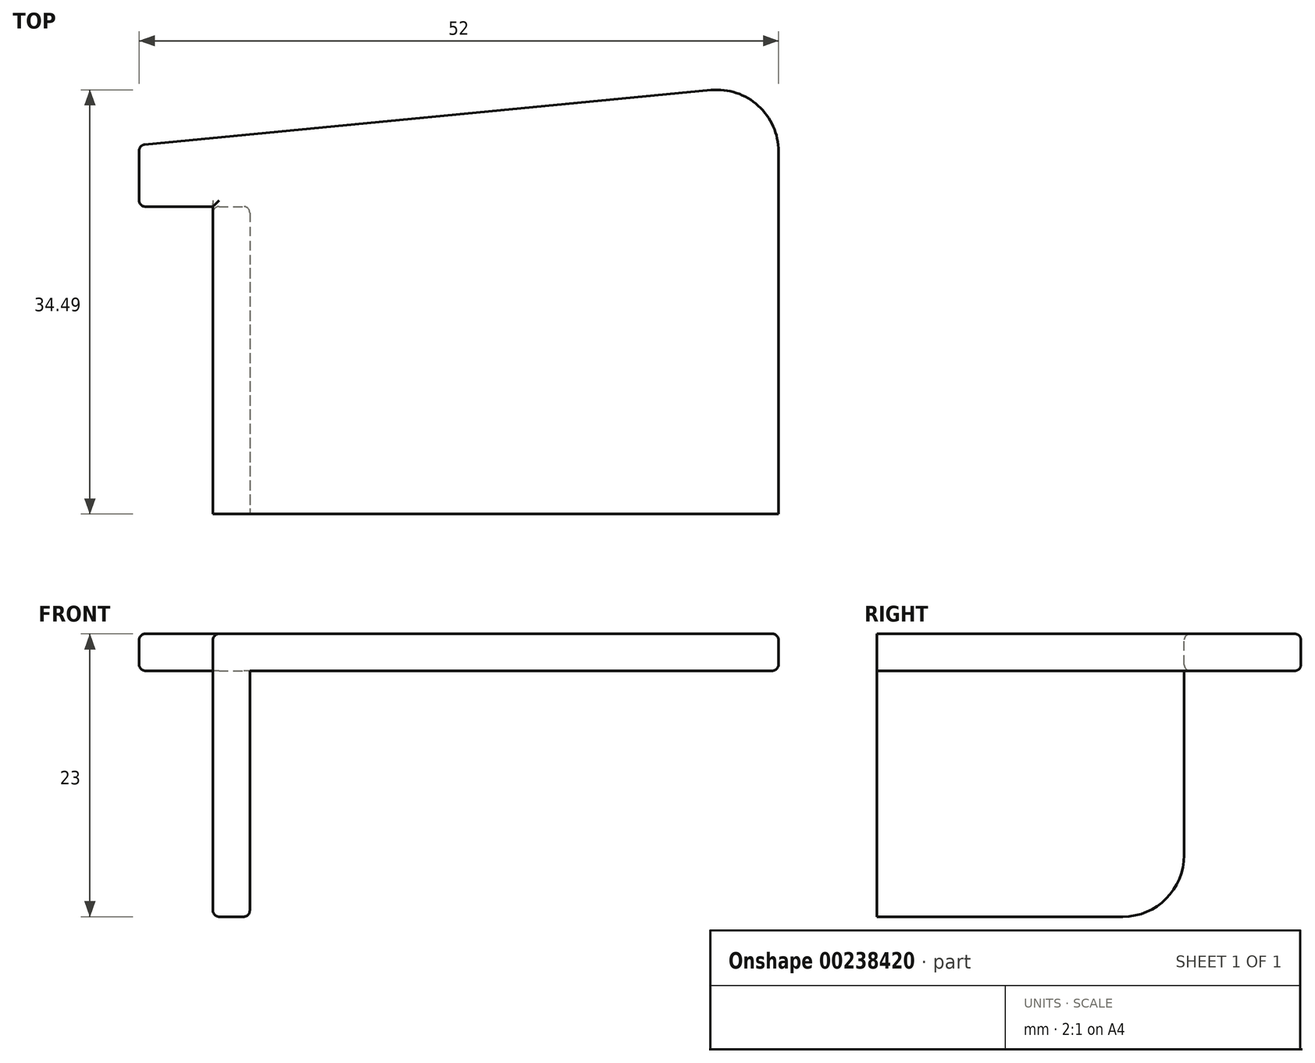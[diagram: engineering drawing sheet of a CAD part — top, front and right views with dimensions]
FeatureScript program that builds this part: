
annotation { "Feature Type Name" : "Feature", "Feature Type Description" : "" }
export const myFeature = defineFeature(function(context is Context, id is Id, definition is map)
    precondition{}
    {
        {
            var Q0;
            Q0=qCreatedBy(makeId("Top.planeOp"),FACE);
            var sketch = newSketch(context, id + "F0", { "sketchPlane" : qUnion([Q0])});
            skLineSegment(sketch, "E0", {"start": v(-20.55, 9.84) * mm, "end": v(-20.55, 4.84) * mm});
            skLineSegment(sketch, "E1", {"start": v(-20.55, 4.84) * mm, "end": v(-14.55, 4.84) * mm});
            skLineSegment(sketch, "E2", {"start": v(-14.55, 4.84) * mm, "end": v(-14.55, -20.16) * mm});
            skLineSegment(sketch, "E3", {"start": v(-14.55, -20.16) * mm, "end": v(31.45, -20.16) * mm});
            skLineSegment(sketch, "E4", {"start": v(31.45, -20.16) * mm, "end": v(31.45, 9.33) * mm});
            skLineSegment(sketch, "E5", {"start": v(-20.55, 9.84) * mm, "end": v(25.97, 14.31) * mm});
            skPoint(sketch, "E6.visualSharp", {"position": v(31.45, 14.84) * mm});
            skArc(sketch, "E6.filletArc", {"start": v(31.45, 9.33) * mm, "mid": v(29.8, 13.03) * mm, "end": v(25.97, 14.31) * mm});
            skLineSegment(sketch, "E7.bottom", {"start": v(-14.55, 4.84) * mm, "end": v(-11.55, 4.84) * mm});
            skLineSegment(sketch, "E7.top", {"start": v(-14.55, -20.16) * mm, "end": v(-11.55, -20.16) * mm});
            skLineSegment(sketch, "E7.right", {"start": v(-11.55, 4.84) * mm, "end": v(-11.55, -20.16) * mm});
            skSolve(sketch);
        }
        {
            var Q0;
            Q0=makeQuery(id+"F0.imprint","IMPRINT",FACE,{"disambiguationData":[TD([[makeQuery(id+"F0.imprint","IMPRINT",EDGE,{"derivedFrom":sQuery(id+"F0.wireOp",EDGE,"E0")}),1.0]])]});
            extrude(context, id + "F1", {"entities" : qUnion([Q0]), "oppositeDirection" : true, "depth" : 3 * mm, "offsetDistance" : 25 * mm});
        }
        {
            var Q0;
            {var subQ0=sQuery(id+"F0.wireOp",EDGE,"E2");Q0=makeQuery(id+"F0.imprint","IMPRINT",FACE,{"disambiguationData":[TD([[makeQuery(id+"F0.imprint","IMPRINT",EDGE,{"derivedFrom":subQ0}),1.0]])]});}
            extrude(context, id + "F2", {"entities" : qUnion([Q0]), "operationType" : NewBodyOperationType.ADD, "oppositeDirection" : true, "depth" : 23 * mm, "offsetDistance" : 25 * mm});
        }
        {
            var Q0;
            Q0=makeQuery(id+"F1.opExtrude","CAP_EDGE",EDGE,{"disambiguationData":[OSD([sQuery(id+"F0.wireOp",EDGE,"E5")])],"isStart":true});
            var Q1;
            Q1=makeQuery(id+"F1.opExtrude","CAP_EDGE",EDGE,{"disambiguationData":[OSD([sQuery(id+"F0.wireOp",EDGE,"E5")])],"isStart":false});
            var Q2;
            Q2=makeQuery(id+"F1.opExtrude","SWEPT_EDGE",EDGE,{"disambiguationData":[OSD([sQuery(id+"F0.wireOp",EDGE,"E0"),sQuery(id+"F0.wireOp",EDGE,"E5")])]});
            var Q3;
            Q3=makeQuery(id+"F1.opExtrude","CAP_EDGE",EDGE,{"disambiguationData":[OSD([sQuery(id+"F0.wireOp",EDGE,"E6.filletArc")])],"isStart":false});
            var Q4;
            Q4=makeQuery(id+"F1.opExtrude","CAP_EDGE",EDGE,{"disambiguationData":[OSD([sQuery(id+"F0.wireOp",EDGE,"E4")])],"isStart":false});
            var Q5;
            Q5=makeQuery(id+"F1.opExtrude","CAP_EDGE",EDGE,{"disambiguationData":[OSD([sQuery(id+"F0.wireOp",EDGE,"E6.filletArc")])],"isStart":true});
            var Q6;
            Q6=makeQuery(id+"F1.opExtrude","CAP_EDGE",EDGE,{"disambiguationData":[OSD([sQuery(id+"F0.wireOp",EDGE,"E4")])],"isStart":true});
            fillet(context, id + "F3", {"entities" : qUnion([Q0, Q1, Q2, Q3, Q4, Q5, Q6]), "radius" : .5 * mm, "tangentPropagation" : true, "allowEdgeOverflow" : false});
        }
        {
            var Q0;
            Q0=makeQuery(id+"F1.opExtrude","CAP_EDGE",EDGE,{"disambiguationData":[OSD([sQuery(id+"F0.wireOp",EDGE,"E7.right")])],"isStart":false});
            var Q1;
            {var subQ0=sQuery(id+"F0.wireOp",EDGE,"E7.bottom");var subQ1=sQuery(id+"F0.wireOp",EDGE,"E1");Q1=makeQuery(id+"F2.boolean.opBoolean","SPLIT",EDGE,{"disambiguationData":[topologyDisambiguationEdgeConnected([makeQuery(id+"F2.opExtrude","SWEPT_FACE",FACE,{"disambiguationData":[OSD([subQ0])]})])],"derivedFrom":makeQuery(id+"F1.opExtrude","CAP_EDGE",EDGE,{"disambiguationData":[OSD([subQ1,subQ0])],"isStart":false})});}
            fillet(context, id + "F4", {"entities" : qUnion([Q0, Q1]), "radius" : .5 * mm, "tangentPropagation" : true, "allowEdgeOverflow" : false});
        }
        {
            var Q0;
            Q0=makeQuery(id+"F2.opExtrude","CAP_EDGE",EDGE,{"disambiguationData":[OSD([sQuery(id+"F0.wireOp",EDGE,"E7.right")])],"isStart":false});
            var Q1;
            Q1=makeQuery(id+"F2.opExtrude","SWEPT_EDGE",EDGE,{"disambiguationData":[OSD([sQuery(id+"F0.wireOp",EDGE,"E7.bottom"),sQuery(id+"F0.wireOp",EDGE,"E7.right")])]});
            var Q2;
            Q2=makeQuery(id+"F2.opExtrude","CAP_EDGE",EDGE,{"disambiguationData":[OSD([sQuery(id+"F0.wireOp",EDGE,"E2")])],"isStart":false});
            var Q3;
            {var subQ0=sQuery(id+"F0.wireOp",EDGE,"E2");var subQ1=sQuery(id+"F0.wireOp",EDGE,"E7.bottom");Q3=makeQuery(id+"F2.boolean.opBoolean","SPLIT",EDGE,{"disambiguationData":[topologyDisambiguationEdgeConnected([makeQuery(id+"F2.opExtrude","SWEPT_FACE",FACE,{"disambiguationData":[OSD([subQ1])]})])],"derivedFrom":makeQuery(id+"F2.opExtrude","SWEPT_EDGE",EDGE,{"disambiguationData":[OSD([sQuery(id+"F0.wireOp",EDGE,"E1"),subQ0,subQ1])]})});}
            fillet(context, id + "F5", {"entities" : qUnion([Q0, Q1, Q2, Q3]), "radius" : .5 * mm, "tangentPropagation" : true, "allowEdgeOverflow" : false});
        }
        {
            var Q0;
            Q0=makeQuery(id+"F1.opExtrude","CAP_EDGE",EDGE,{"disambiguationData":[OSD([sQuery(id+"F0.wireOp",EDGE,"E1"),sQuery(id+"F0.wireOp",EDGE,"E7.bottom")])],"isStart":true});
            var Q1;
            Q1=makeQuery(id+"F1.opExtrude","CAP_EDGE",EDGE,{"disambiguationData":[OSD([sQuery(id+"F0.wireOp",EDGE,"E0")])],"isStart":true});
            var Q2;
            {var subQ0=sQuery(id+"F0.wireOp",EDGE,"E7.bottom");var subQ1=sQuery(id+"F0.wireOp",EDGE,"E1");Q2=makeQuery(id+"F2.boolean.opBoolean","SPLIT",EDGE,{"disambiguationData":[topologyDisambiguationEdgeConnected([makeQuery(id+"F1.opExtrude","SWEPT_FACE",FACE,{"disambiguationData":[OSD([subQ1,subQ0])]})])],"derivedFrom":makeQuery(id+"F1.opExtrude","CAP_EDGE",EDGE,{"disambiguationData":[OSD([subQ1,subQ0])],"isStart":false})});}
            var Q3;
            Q3=makeQuery(id+"F1.opExtrude","CAP_EDGE",EDGE,{"disambiguationData":[OSD([sQuery(id+"F0.wireOp",EDGE,"E0")])],"isStart":false});
            var Q4;
            Q4=makeQuery(id+"F1.opExtrude","SWEPT_EDGE",EDGE,{"disambiguationData":[OSD([sQuery(id+"F0.wireOp",EDGE,"E0"),sQuery(id+"F0.wireOp",EDGE,"E1")])]});
            fillet(context, id + "F6", {"entities" : qUnion([Q0, Q1, Q2, Q3, Q4]), "radius" : .5 * mm, "tangentPropagation" : true, "allowEdgeOverflow" : false});
        }
        {
            var Q0;
            Q0=makeQuery(id+"F2.opExtrude","CAP_EDGE",EDGE,{"disambiguationData":[OSD([sQuery(id+"F0.wireOp",EDGE,"E2")])],"isStart":true});
            fillet(context, id + "F7", {"entities" : qUnion([Q0]), "radius" : .5 * mm, "tangentPropagation" : true, "allowEdgeOverflow" : false});
        }
        {
            var Q0;
            Q0=makeQuery(id+"F2.opExtrude","CAP_EDGE",EDGE,{"disambiguationData":[OSD([sQuery(id+"F0.wireOp",EDGE,"E7.bottom")])],"isStart":false});
            fillet(context, id + "F8", {"entities" : qUnion([Q0]), "radius" : 5 * mm, "tangentPropagation" : true, "allowEdgeOverflow" : false});
        }
    });
